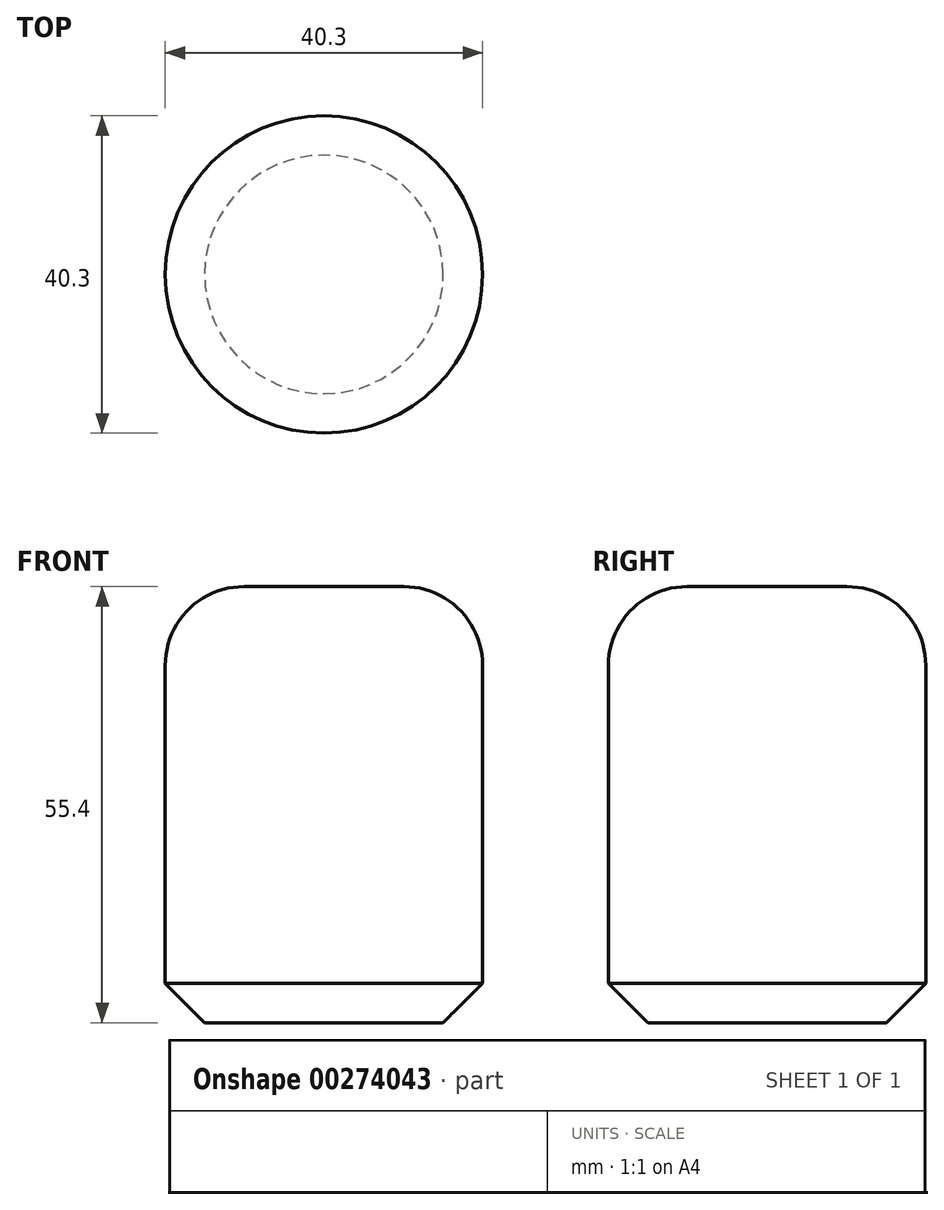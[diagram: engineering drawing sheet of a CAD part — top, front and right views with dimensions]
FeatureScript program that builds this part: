
annotation { "Feature Type Name" : "Feature", "Feature Type Description" : "" }
export const myFeature = defineFeature(function(context is Context, id is Id, definition is map)
    precondition{}
    {
        {
            var Q0;
            Q0=qCreatedBy(makeId("Top.planeOp"),FACE);
            var sketch = newSketch(context, id + "F0", { "sketchPlane" : qUnion([Q0])});
            skCircle(sketch, "E0", {"center": v(0, 0) * mm, "radius": 20.15 * mm});
            skSolve(sketch);
        }
        {
            var Q0;
            Q0=makeQuery(id+"F0.imprint","IMPRINT",FACE,{"disambiguationData":[TD([[makeQuery(id+"F0.imprint","IMPRINT",EDGE,{"derivedFrom":sQuery(id+"F0.wireOp",EDGE,"E0")}),1.0]])]});
            extrude(context, id + "F1", {"entities" : qUnion([Q0]), "depth" : 25.4 * mm});
        }
        {
            var Q0;
            Q0=makeQuery(id+"F1.opExtrude","CAP_FACE",FACE,{"disambiguationData":[OSD([sQuery(id+"F0.wireOp",EDGE,"E0")])],"isStart":false});
            extrude(context, id + "F2", {"entities" : qUnion([Q0]), "operationType" : NewBodyOperationType.ADD, "depth" : 30 * mm});
        }
        {
            var Q0;
            Q0=makeQuery(id+"F2.opExtrude","CAP_FACE",FACE,{"disambiguationData":[OSD([sQuery(id+"F0.wireOp",EDGE,"E0")])],"isStart":false});
            fillet(context, id + "F3", {"entities" : qUnion([Q0]), "radius" : 10 * mm, "tangentPropagation" : true, "allowEdgeOverflow" : false});
        }
        {
            var Q0;
            Q0=makeQuery(id+"F1.opExtrude","CAP_FACE",FACE,{"disambiguationData":[OSD([sQuery(id+"F0.wireOp",EDGE,"E0")])],"isStart":true});
            chamfer(context, id + "F4", {"entities" : qUnion([Q0]), "width" : 5 * mm, "tangentPropagation" : true});
        }
    });
